# Revit family: IS_Iom_A7928_BIM_NL
name_source: partatom
category: Plumbing Fixtures
units: mm (PartAtom-declared; Revit-internal decimal feet)

## family parameters
Always vertical = No
Cut with Voids When Loaded = No
OmniClass Number = 23.45.05.14.21.11
OmniClass Title = Bath/Shower Units
Part Type = Normal
Room Calculation Point = No
Round Connector Dimension = Use Diameter
Shared = No
Work Plane-Based = No

## types (1)
- A7928XG - Iom Tumbler Black Glass & Holder Wall Mounted - Silk Black
    Accessories = http://www.idealstandard.nl
    Afmetingen = 69 x 105 x 96 mm
    AfstandsEenheid = Millimeter
    Afwerking = Seidenschwarz
    AreaUnits = millimetres
    Artikelnummer = A7928XG
    Artikelomschrijving = Iom Tumbler Schwarzes Glas & Halter Wandmontage - Seidenschwarz
    AssetType = Fixed
    Auteur = Ideal Standard
    BIMObjectName = IS_IdealStandard_SanitaryAccessories_IOM_A7928
    BIMobject category = Sanitary: Toilet Accssories
    BIMobject main category = Sanitary
    BIMobject main category code = Sanitary
    BarCode = 4015413356435
    Beschrijvinggarantie = Herstellergarantie
    Bestanddelen = http://www.idealstandard.nl
    BimObjectNaam = IS_IdealStandard_SanitaryAccessories_IOM_A7928
    Brand = Ideal Standard
    Brand url = http://www.idealstandard.nl
    Breedte = 69.076664
    BrutoGewicht = 0
    Category = Plumbing
    Classification = Sanitary
    Color = Silk Black
    ConnectionType = Plumbing
    Cost = 0 $
    CurrencyUnit = €
    CurrentRevision = 1
    Date of publishing = 24/01/2023
    Description = Iom Tumbler Black Glass & Holder Wall Mounted - Silk Black
    Diepte = 105 mm
    DurationUnit = Years
    DuurEenheid = Jahr
    Edition number = 1
    ElementType = Sanitary Accessories
    Features = Tumbler Black Glass & Holder Wall Mounted - Silk Black
    Finish = Silk Black
    GTIN code = 4015413356435
    Garantieunits = Jahre
    GemaaktOp = 24/01/2023
    Help = http://www.idealstandard.nl
    Hoogte = 96.004976272583
    IFC Classification = Sanitary Terminal
    IfcExportAs = IfcFurnitureType
    IfcExportType = BRUSHHOLDER
    Installatieinstructies = http://www.idealstandard.nl
    Installation instructions = http://www.idealstandard.nl
    InstallationInstructions = http://www.idealstandard.nl
    Kleur = Seidenschwarz
    Lengte = 105 mm
    LinearUnits = millimeters
    MainColor = Silk Black
    MaintenanceInformation = http://www.idealstandard.nl
    Manufacturer = Ideal Standard
    Manufacturer name = Ideal Standard
    ManufacturerURL = http://www.idealstandard.nl
    Materiaal = schwarzes Glas und Metall
    Material = black glass&metal
    Material main = black glass&metal
    Merk = Ideal Standard
    Model = A7928XG
    ModelNumber = A7928XG
    ModelReference = Iom Tumbler Black Glass & Holder Wall Mounted
    NBS Reference Code = 45-35-72/376
    NBS Reference Description = Tumbler holders
    Name = SanitaryAccessories_IOM_A7928_IdealStandard
    NettWeight = 0.001
    Nettogewicht = 0.001
    NominalDepth = 105 mm
    NominalHeight = 96 mm
    NominalLength = 105 mm
    NominalWidth = 69 mm
    OppervlakteAfmeting = Millimeter
    OppervlakteEenheid = Millimeter
    PredefinedType = Sanitary Accessories
    Product Guid = 52d123f9-3faa-42a0-acb2-2d5c910eb260
    Product SKU = A7928
    Product certification = http://www.idealstandard.nl
    Product data url = https://bimobject.com
    Product family = Iom
    Product group = Accessories
    Product name = Iom Tumbler Black Glass & Holder Wall Mounted
    Product url = http://www.idealstandard.nl
    ProductInformation = http://www.idealstandard.nl
    Productinformatie = http://www.idealstandard.nl
    QR code = http://bimobject.com
    Revisie = 1
    Shape = cilindrical
    Size = 69 x 105 x 96 mm
    Space = Internal
    SpareParts = http://www.idealstandard.nl
    Technical description = http://www.idealstandard.nl
    Telefoonnummer = 077 355 08 08
    Typeconnectie = Installation
    UNSPSC Code = 30181500
    URL = http://www.idealstandard.nl
    Uniclass 1.4 Code = N14
    Uniclass 1.4 Description = Accessories
    Uniclass 2015 Code = Pr_40_20_76
    Uniclass 2015 Name = Sanitary accessories
    Uniclass2015Beschrijving = Sanitary accessories
    Uniclass2015Code = Pr_40_20_76
    Uniclass2015Referentie = Sanitary accessories
    Uniclass2015Title = Sanitary accessories
    Uniclass2015Version = V1.26
    Uniformat II Code = C1030
    Uniformat II Description = Fittings
    Urlproducent = http://www.idealstandard.nl
    ValutaEenheid = €
    Versie = 1
    Version = 1
    Vervangingskosten = 0
    VolumeUnits = Liters
    Volumeunits = Liter
    Vorm = Zylinder
    WRASURL = https://www.wrasapprovals.co.uk
    WarrantyDescription = Manufacturers Warranty
    WarrantyDurationUnit = Years
    Weight Net (Kg) = 0.001
    Wisselstukken = http://www.idealstandard.nl
    Youtube clip = https://www.youtube.com

## geometry (parser evidence)
native form markers: Sweep x2
no freeform markers — native parametric forms only
